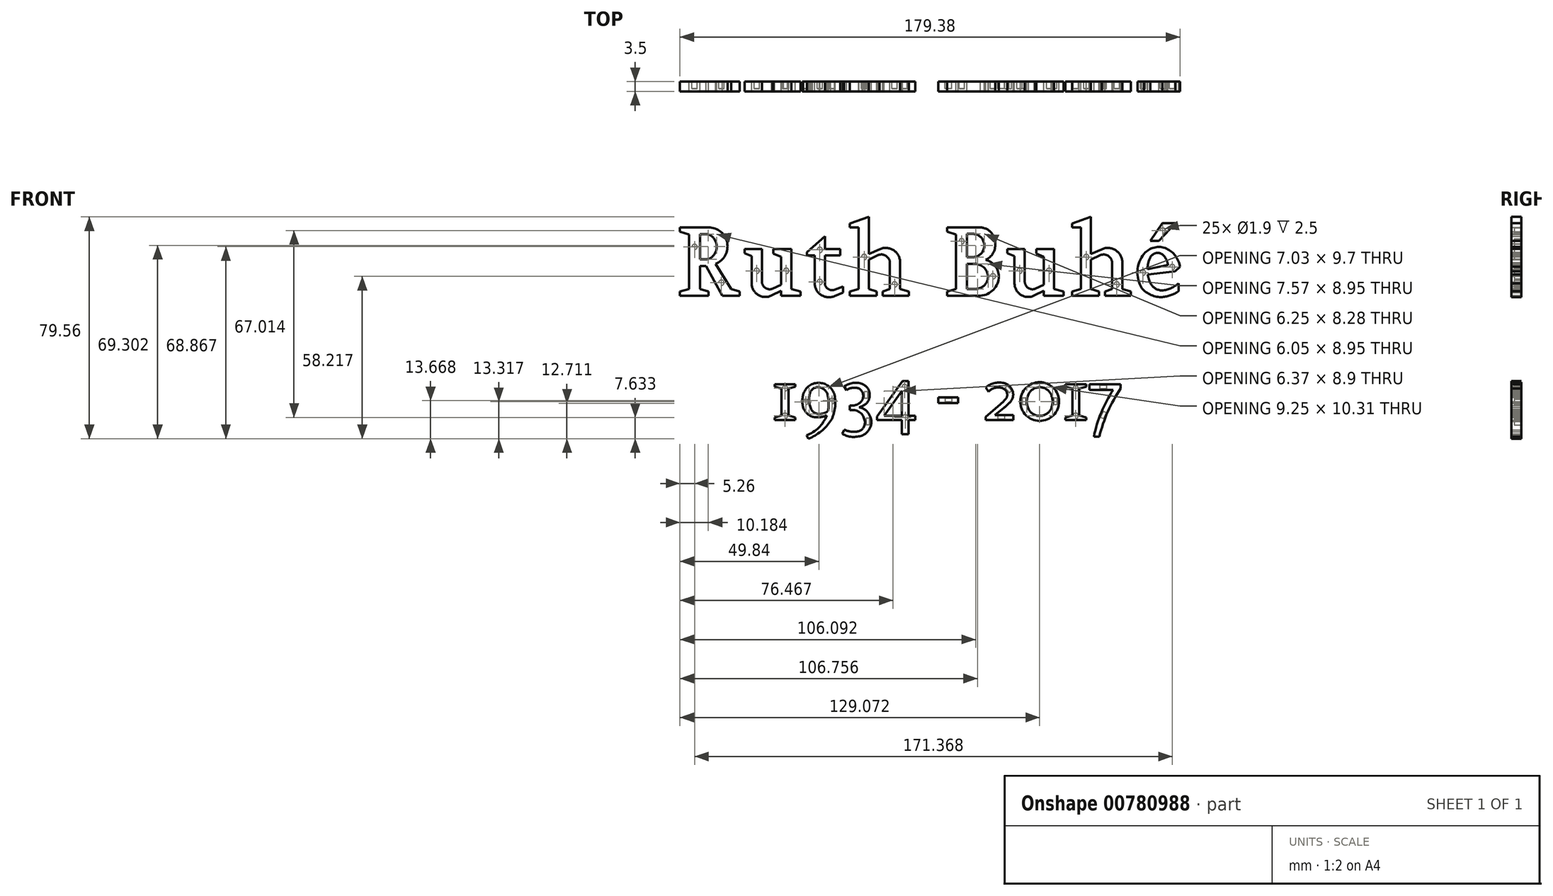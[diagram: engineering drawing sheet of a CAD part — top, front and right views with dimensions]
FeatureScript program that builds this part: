
annotation { "Feature Type Name" : "Feature", "Feature Type Description" : "" }
export const myFeature = defineFeature(function(context is Context, id is Id, definition is map)
    precondition{}
    {
        {
            var Q0;
            Q0=qCreatedBy(makeId("Front.planeOp"),FACE);
            var sketch = newSketch(context, id + "F0", { "sketchPlane" : qUnion([Q0])});
            skSolve(sketch);
        }
        {
            var Q0;
            Q0=qCreatedBy(makeId("Front.planeOp"),FACE);
            var sketch = newSketch(context, id + "F1", { "sketchPlane" : qUnion([Q0])});
            skLineSegment(sketch, "E0", {"start": v(-78.02, 15.2) * mm, "end": v(-67.8, 15.2) * mm});
            skLineSegment(sketch, "E1", {"start": v(-67.8, 15.2) * mm, "end": v(-67.8, 16.73) * mm});
            skLineSegment(sketch, "E2", {"start": v(-67.8, 16.73) * mm, "end": v(-70.86, 17.67) * mm});
            skLineSegment(sketch, "E3", {"start": v(-70.86, 17.67) * mm, "end": v(-70.86, 25.9) * mm});
            skLineSegment(sketch, "E4", {"start": v(-70.86, 25.9) * mm, "end": v(-68.64, 25.9) * mm});
            skLineSegment(sketch, "E5", {"start": v(-68.64, 25.9) * mm, "end": v(-62.81, 15.2) * mm});
            skLineSegment(sketch, "E6", {"start": v(-62.81, 15.2) * mm, "end": v(-56.63, 15.2) * mm});
            skLineSegment(sketch, "E7", {"start": v(-56.63, 15.2) * mm, "end": v(-56.63, 16.73) * mm});
            skLineSegment(sketch, "E8", {"start": v(-56.63, 16.73) * mm, "end": v(-59.61, 17.67) * mm});
            skLineSegment(sketch, "E9", {"start": v(-59.61, 17.67) * mm, "end": v(-65.23, 26.62) * mm});
            skLineSegment(sketch, "E10", {"start": v(-78.02, 15.2) * mm, "end": v(-78.02, 16.73) * mm});
            skLineSegment(sketch, "E11", {"start": v(-78.02, 16.73) * mm, "end": v(-74.74, 17.67) * mm});
            skLineSegment(sketch, "E12", {"start": v(-74.74, 17.67) * mm, "end": v(-74.74, 37.23) * mm});
            skLineSegment(sketch, "E13", {"start": v(-74.74, 37.23) * mm, "end": v(-78.02, 38.21) * mm});
            skLineSegment(sketch, "E14", {"start": v(-78.02, 38.21) * mm, "end": v(-78.02, 39.74) * mm});
            skLineSegment(sketch, "E15", {"start": v(-78.02, 39.74) * mm, "end": v(-68.86, 39.74) * mm});
            skArc(sketch, "E16", {"start": v(-65.23, 26.62) * mm, "mid": v(-61.06, 34.23) * mm, "end": v(-67.76, 39.74) * mm});
            skArc(sketch, "E17", {"start": v(-67.74, 28.32) * mm, "mid": v(-64.81, 32.8) * mm, "end": v(-67.74, 37.27) * mm});
            skLineSegment(sketch, "E18", {"start": v(-67.74, 37.27) * mm, "end": v(-70.86, 37.27) * mm});
            skLineSegment(sketch, "E19", {"start": v(-70.86, 37.27) * mm, "end": v(-70.86, 28.32) * mm});
            skLineSegment(sketch, "E20", {"start": v(-70.86, 28.32) * mm, "end": v(-67.74, 28.32) * mm});
            skLineSegment(sketch, "E21", {"start": v(-68.86, 39.74) * mm, "end": v(-67.76, 39.74) * mm});
            skSolve(sketch);
        }
        {
            var Q0;
            Q0=makeQuery(id+"F1.imprint","IMPRINT",FACE,{"disambiguationData":[TD([[makeQuery(id+"F1.imprint","IMPRINT",EDGE,{"derivedFrom":sQuery(id+"F1.wireOp",EDGE,"E0")}),1.0]])]});
            extrude(context, id + "F2", {"entities" : qUnion([Q0]), "depth" : 3.5 * mm, "offsetDistance" : 25 * mm});
        }
        {
            var Q0;
            Q0=makeQuery(id+"F2.opExtrude","SWEPT_EDGE",EDGE,{"disambiguationData":[OSD([sQuery(id+"F1.wireOp",EDGE,"E17"),sQuery(id+"F1.wireOp",EDGE,"E18")])]});
            var Q1;
            Q1=makeQuery(id+"F2.opExtrude","SWEPT_EDGE",EDGE,{"disambiguationData":[OSD([sQuery(id+"F1.wireOp",EDGE,"E17"),sQuery(id+"F1.wireOp",EDGE,"E20")])]});
            fillet(context, id + "F3", {"entities" : qUnion([Q0, Q1]), "radius" : 3 * mm, "tangentPropagation" : true, "allowEdgeOverflow" : false});
        }
        {
            var Q0;
            Q0=makeQuery(id+"F2.opExtrude","CAP_FACE",FACE,{"disambiguationData":[OSD([sQuery(id+"F1.wireOp",EDGE,"E0"),sQuery(id+"F1.wireOp",EDGE,"E1"),sQuery(id+"F1.wireOp",EDGE,"E2"),sQuery(id+"F1.wireOp",EDGE,"E3"),sQuery(id+"F1.wireOp",EDGE,"E4"),sQuery(id+"F1.wireOp",EDGE,"E5"),sQuery(id+"F1.wireOp",EDGE,"E6"),sQuery(id+"F1.wireOp",EDGE,"E7"),sQuery(id+"F1.wireOp",EDGE,"E8"),sQuery(id+"F1.wireOp",EDGE,"E9"),sQuery(id+"F1.wireOp",EDGE,"E10"),sQuery(id+"F1.wireOp",EDGE,"E11"),sQuery(id+"F1.wireOp",EDGE,"E12"),sQuery(id+"F1.wireOp",EDGE,"E13"),sQuery(id+"F1.wireOp",EDGE,"E14"),sQuery(id+"F1.wireOp",EDGE,"E15"),sQuery(id+"F1.wireOp",EDGE,"E16"),sQuery(id+"F1.wireOp",EDGE,"E17"),sQuery(id+"F1.wireOp",EDGE,"E18"),sQuery(id+"F1.wireOp",EDGE,"E19"),sQuery(id+"F1.wireOp",EDGE,"E20"),sQuery(id+"F1.wireOp",EDGE,"E21")])],"isStart":true});
            var sketch = newSketch(context, id + "F4", { "sketchPlane" : qUnion([Q0])});
            skCircle(sketch, "E22", {"center": v(72.76, 32.74) * mm, "radius": 0.95 * mm});
            skCircle(sketch, "E23", {"center": v(63.13, 19.9) * mm, "radius": 0.95 * mm});
            skSolve(sketch);
        }
        {
            var Q0;
            Q0=makeQuery(id+"F4.imprint","IMPRINT",FACE,{"disambiguationData":[TD([[makeQuery(id+"F4.imprint","IMPRINT",EDGE,{"derivedFrom":sQuery(id+"F4.wireOp",EDGE,"E22")}),1.0]])]});
            var Q1;
            Q1=makeQuery(id+"F4.imprint","IMPRINT",FACE,{"disambiguationData":[TD([[makeQuery(id+"F4.imprint","IMPRINT",EDGE,{"derivedFrom":sQuery(id+"F4.wireOp",EDGE,"E23")}),1.0]])]});
            extrude(context, id + "F5", {"entities" : qUnion([Q0, Q1]), "operationType" : NewBodyOperationType.REMOVE, "oppositeDirection" : true, "depth" : 2.5 * mm, "offsetDistance" : 25 * mm});
        }
        {
            var Q0;
            Q0=qCreatedBy(makeId("Front.planeOp"),FACE);
            var sketch = newSketch(context, id + "F6", { "sketchPlane" : qUnion([Q0])});
            skLineSegment(sketch, "E24", {"start": v(-41.77, 15.2) * mm, "end": v(-34.7, 15.2) * mm});
            skLineSegment(sketch, "E25", {"start": v(-34.7, 15.2) * mm, "end": v(-34.7, 16.73) * mm});
            skLineSegment(sketch, "E26", {"start": v(-34.7, 16.73) * mm, "end": v(-38.08, 17.67) * mm});
            skLineSegment(sketch, "E27", {"start": v(-38.08, 17.67) * mm, "end": v(-38.08, 32) * mm});
            skLineSegment(sketch, "E28", {"start": v(-38.08, 32) * mm, "end": v(-44.47, 32) * mm});
            skLineSegment(sketch, "E29", {"start": v(-44.47, 32) * mm, "end": v(-44.47, 30.27) * mm});
            skLineSegment(sketch, "E30", {"start": v(-44.47, 30.27) * mm, "end": v(-41.77, 29.18) * mm});
            skLineSegment(sketch, "E31", {"start": v(-41.77, 29.18) * mm, "end": v(-41.77, 19.11) * mm});
            skLineSegment(sketch, "E32", {"start": v(-41.77, 15.2) * mm, "end": v(-41.77, 16.98) * mm});
            skLineSegment(sketch, "E33", {"start": v(-41.77, 16.98) * mm, "end": v(-45.17, 15.3) * mm});
            skLineSegment(sketch, "E34", {"start": v(-41.77, 19.11) * mm, "end": v(-44.76, 17.72) * mm});
            skLineSegment(sketch, "E35", {"start": v(-52.26, 19.48) * mm, "end": v(-52.26, 29.48) * mm});
            skLineSegment(sketch, "E36", {"start": v(-52.26, 29.48) * mm, "end": v(-54.82, 30.46) * mm});
            skLineSegment(sketch, "E37", {"start": v(-54.82, 30.46) * mm, "end": v(-54.82, 32) * mm});
            skLineSegment(sketch, "E38", {"start": v(-54.82, 32) * mm, "end": v(-48.6, 32) * mm});
            skLineSegment(sketch, "E39", {"start": v(-48.6, 32) * mm, "end": v(-48.6, 20.2) * mm});
            skArc(sketch, "E40", {"start": v(-52.26, 19.48) * mm, "mid": v(-49.87, 15.44) * mm, "end": v(-45.17, 15.3) * mm});
            skArc(sketch, "E41", {"start": v(-48.6, 20.2) * mm, "mid": v(-47.31, 17.98) * mm, "end": v(-44.76, 17.72) * mm});
            skSolve(sketch);
        }
        {
            var Q0;
            Q0=makeQuery(id+"F6.imprint","IMPRINT",FACE,{"disambiguationData":[TD([[makeQuery(id+"F6.imprint","IMPRINT",EDGE,{"derivedFrom":sQuery(id+"F6.wireOp",EDGE,"E24")}),1.0]])]});
            extrude(context, id + "F7", {"entities" : qUnion([Q0]), "depth" : 3.5 * mm, "offsetDistance" : 25 * mm});
        }
        {
            var Q0;
            Q0=makeQuery(id+"F7.opExtrude","CAP_FACE",FACE,{"disambiguationData":[OSD([sQuery(id+"F6.wireOp",EDGE,"E24"),sQuery(id+"F6.wireOp",EDGE,"E25"),sQuery(id+"F6.wireOp",EDGE,"E26"),sQuery(id+"F6.wireOp",EDGE,"E27"),sQuery(id+"F6.wireOp",EDGE,"E28"),sQuery(id+"F6.wireOp",EDGE,"E29"),sQuery(id+"F6.wireOp",EDGE,"E30"),sQuery(id+"F6.wireOp",EDGE,"E31"),sQuery(id+"F6.wireOp",EDGE,"E32"),sQuery(id+"F6.wireOp",EDGE,"E33"),sQuery(id+"F6.wireOp",EDGE,"E34"),sQuery(id+"F6.wireOp",EDGE,"E35"),sQuery(id+"F6.wireOp",EDGE,"E36"),sQuery(id+"F6.wireOp",EDGE,"E37"),sQuery(id+"F6.wireOp",EDGE,"E38"),sQuery(id+"F6.wireOp",EDGE,"E39"),sQuery(id+"F6.wireOp",EDGE,"E40"),sQuery(id+"F6.wireOp",EDGE,"E41")])],"isStart":true});
            var sketch = newSketch(context, id + "F8", { "sketchPlane" : qUnion([Q0])});
            skCircle(sketch, "E42", {"center": v(50.45, 24.15) * mm, "radius": 0.95 * mm});
            skCircle(sketch, "E43", {"center": v(39.88, 24.15) * mm, "radius": 0.95 * mm});
            skPoint(sketch, "E43.centerSnap0", {"position": v(41.77, 24.15) * mm});
            skSolve(sketch);
        }
        {
            var Q0;
            Q0=makeQuery(id+"F8.imprint","IMPRINT",FACE,{"disambiguationData":[TD([[makeQuery(id+"F8.imprint","IMPRINT",EDGE,{"derivedFrom":sQuery(id+"F8.wireOp",EDGE,"E43")}),1.0]])]});
            var Q1;
            Q1=makeQuery(id+"F8.imprint","IMPRINT",FACE,{"disambiguationData":[TD([[makeQuery(id+"F8.imprint","IMPRINT",EDGE,{"derivedFrom":sQuery(id+"F8.wireOp",EDGE,"E42")}),1.0]])]});
            extrude(context, id + "F9", {"entities" : qUnion([Q0, Q1]), "operationType" : NewBodyOperationType.REMOVE, "oppositeDirection" : true, "depth" : 2.5 * mm, "offsetDistance" : 25 * mm});
        }
        {
            var Q0;
            Q0=qCreatedBy(makeId("Front.planeOp"),FACE);
            var sketch = newSketch(context, id + "F10", { "sketchPlane" : qUnion([Q0])});
            skLineSegment(sketch, "E44", {"start": v(-20.57, 32) * mm, "end": v(-26.02, 32) * mm});
            skLineSegment(sketch, "E45", {"start": v(-26.02, 32) * mm, "end": v(-26.02, 36.51) * mm});
            skLineSegment(sketch, "E46", {"start": v(-26.02, 36.51) * mm, "end": v(-32.46, 30.8) * mm});
            skLineSegment(sketch, "E47", {"start": v(-32.46, 30.8) * mm, "end": v(-32.46, 29.66) * mm});
            skLineSegment(sketch, "E48", {"start": v(-32.46, 29.66) * mm, "end": v(-29.69, 29.66) * mm});
            skLineSegment(sketch, "E49", {"start": v(-29.69, 29.66) * mm, "end": v(-29.69, 19.66) * mm});
            skLineSegment(sketch, "E50", {"start": v(-20.57, 32) * mm, "end": v(-20.57, 29.66) * mm});
            skLineSegment(sketch, "E51", {"start": v(-20.57, 29.66) * mm, "end": v(-26.02, 29.66) * mm});
            skLineSegment(sketch, "E52", {"start": v(-26.02, 29.66) * mm, "end": v(-26.02, 19.66) * mm});
            skLineSegment(sketch, "E53", {"start": v(-22.55, 17.37) * mm, "end": v(-19.53, 18.45) * mm});
            skLineSegment(sketch, "E54", {"start": v(-19.53, 18.45) * mm, "end": v(-19.53, 16.4) * mm});
            skLineSegment(sketch, "E55", {"start": v(-19.53, 16.4) * mm, "end": v(-22.56, 15.09) * mm});
            skArc(sketch, "E56", {"start": v(-29.69, 19.66) * mm, "mid": v(-27.34, 15.48) * mm, "end": v(-22.56, 15.09) * mm});
            skArc(sketch, "E57", {"start": v(-26.02, 19.66) * mm, "mid": v(-24.85, 17.65) * mm, "end": v(-22.55, 17.37) * mm});
            skSolve(sketch);
        }
        {
            var Q0;
            Q0=makeQuery(id+"F10.imprint","IMPRINT",FACE,{"disambiguationData":[TD([[makeQuery(id+"F10.imprint","IMPRINT",EDGE,{"derivedFrom":sQuery(id+"F10.wireOp",EDGE,"E44")}),1.0]])]});
            extrude(context, id + "F11", {"entities" : qUnion([Q0]), "depth" : 3.5 * mm, "offsetDistance" : 25 * mm});
        }
        {
            var Q0;
            Q0=makeQuery(id+"F11.opExtrude","CAP_FACE",FACE,{"disambiguationData":[OSD([sQuery(id+"F10.wireOp",EDGE,"E44"),sQuery(id+"F10.wireOp",EDGE,"E45"),sQuery(id+"F10.wireOp",EDGE,"E46"),sQuery(id+"F10.wireOp",EDGE,"E47"),sQuery(id+"F10.wireOp",EDGE,"E48"),sQuery(id+"F10.wireOp",EDGE,"E49"),sQuery(id+"F10.wireOp",EDGE,"E50"),sQuery(id+"F10.wireOp",EDGE,"E51"),sQuery(id+"F10.wireOp",EDGE,"E52"),sQuery(id+"F10.wireOp",EDGE,"E53"),sQuery(id+"F10.wireOp",EDGE,"E54"),sQuery(id+"F10.wireOp",EDGE,"E55"),sQuery(id+"F10.wireOp",EDGE,"E56"),sQuery(id+"F10.wireOp",EDGE,"E57")])],"isStart":true});
            var sketch = newSketch(context, id + "F12", { "sketchPlane" : qUnion([Q0])});
            skCircle(sketch, "E58", {"center": v(27.83, 31.66) * mm, "radius": 0.95 * mm});
            skCircle(sketch, "E59", {"center": v(27.83, 20.16) * mm, "radius": 0.95 * mm});
            skSolve(sketch);
        }
        {
            var Q0;
            Q0=makeQuery(id+"F12.imprint","IMPRINT",FACE,{"disambiguationData":[TD([[makeQuery(id+"F12.imprint","IMPRINT",EDGE,{"derivedFrom":sQuery(id+"F12.wireOp",EDGE,"E58")}),1.0]])]});
            var Q1;
            Q1=makeQuery(id+"F12.imprint","IMPRINT",FACE,{"disambiguationData":[TD([[makeQuery(id+"F12.imprint","IMPRINT",EDGE,{"derivedFrom":sQuery(id+"F12.wireOp",EDGE,"E59")}),1.0]])]});
            extrude(context, id + "F13", {"entities" : qUnion([Q0, Q1]), "operationType" : NewBodyOperationType.REMOVE, "oppositeDirection" : true, "depth" : 2.5 * mm, "offsetDistance" : 25 * mm});
        }
        {
            var Q0;
            Q0=qCreatedBy(makeId("Front.planeOp"),FACE);
            var sketch = newSketch(context, id + "F14", { "sketchPlane" : qUnion([Q0])});
            skLineSegment(sketch, "E60", {"start": v(-17.06, 15.2) * mm, "end": v(-7.42, 15.2) * mm});
            skLineSegment(sketch, "E61", {"start": v(-7.42, 15.2) * mm, "end": v(-7.42, 16.73) * mm});
            skLineSegment(sketch, "E62", {"start": v(-7.42, 16.73) * mm, "end": v(-10.26, 17.67) * mm});
            skLineSegment(sketch, "E63", {"start": v(-10.26, 17.67) * mm, "end": v(-10.26, 28.2) * mm});
            skLineSegment(sketch, "E64", {"start": v(-10.26, 28.2) * mm, "end": v(-6.9, 29.76) * mm});
            skLineSegment(sketch, "E65", {"start": v(-17.06, 15.2) * mm, "end": v(-17.06, 16.73) * mm});
            skLineSegment(sketch, "E66", {"start": v(-17.06, 16.73) * mm, "end": v(-13.88, 17.67) * mm});
            skLineSegment(sketch, "E67", {"start": v(-13.88, 17.67) * mm, "end": v(-13.88, 39.74) * mm});
            skLineSegment(sketch, "E68", {"start": v(-13.88, 39.74) * mm, "end": v(-17.06, 39.74) * mm});
            skLineSegment(sketch, "E69", {"start": v(-17.06, 39.74) * mm, "end": v(-17.06, 41.1) * mm});
            skLineSegment(sketch, "E70", {"start": v(-17.06, 41.1) * mm, "end": v(-10.26, 43.5) * mm});
            skLineSegment(sketch, "E71", {"start": v(-10.26, 43.5) * mm, "end": v(-10.26, 30.24) * mm});
            skLineSegment(sketch, "E72", {"start": v(-10.26, 30.24) * mm, "end": v(-6.4, 31.9) * mm});
            skLineSegment(sketch, "E73", {"start": v(-2.67, 27.17) * mm, "end": v(-2.67, 17.67) * mm});
            skLineSegment(sketch, "E74", {"start": v(-2.67, 17.67) * mm, "end": v(-5.22, 16.73) * mm});
            skLineSegment(sketch, "E75", {"start": v(-5.22, 16.73) * mm, "end": v(-5.22, 15.2) * mm});
            skLineSegment(sketch, "E76", {"start": v(-5.22, 15.2) * mm, "end": v(4.1, 15.2) * mm});
            skLineSegment(sketch, "E77", {"start": v(4.1, 15.2) * mm, "end": v(4.1, 16.73) * mm});
            skLineSegment(sketch, "E78", {"start": v(4.1, 16.73) * mm, "end": v(0.99, 17.67) * mm});
            skLineSegment(sketch, "E79", {"start": v(0.99, 17.67) * mm, "end": v(0.99, 27.07) * mm});
            skArc(sketch, "E80", {"start": v(0.99, 27.07) * mm, "mid": v(-1.37, 31.53) * mm, "end": v(-6.4, 31.9) * mm});
            skArc(sketch, "E81", {"start": v(-2.67, 27.17) * mm, "mid": v(-4.12, 29.56) * mm, "end": v(-6.9, 29.76) * mm});
            skSolve(sketch);
        }
        {
            var Q0;
            Q0=makeQuery(id+"F14.imprint","IMPRINT",FACE,{"disambiguationData":[TD([[makeQuery(id+"F14.imprint","IMPRINT",EDGE,{"derivedFrom":sQuery(id+"F14.wireOp",EDGE,"E60")}),1.0]])]});
            extrude(context, id + "F15", {"entities" : qUnion([Q0]), "depth" : 3.5 * mm, "offsetDistance" : 25 * mm});
        }
        {
            var Q0;
            Q0=makeQuery(id+"F15.opExtrude","CAP_FACE",FACE,{"disambiguationData":[OSD([sQuery(id+"F14.wireOp",EDGE,"E60"),sQuery(id+"F14.wireOp",EDGE,"E61"),sQuery(id+"F14.wireOp",EDGE,"E62"),sQuery(id+"F14.wireOp",EDGE,"E63"),sQuery(id+"F14.wireOp",EDGE,"E64"),sQuery(id+"F14.wireOp",EDGE,"E65"),sQuery(id+"F14.wireOp",EDGE,"E66"),sQuery(id+"F14.wireOp",EDGE,"E67"),sQuery(id+"F14.wireOp",EDGE,"E68"),sQuery(id+"F14.wireOp",EDGE,"E69"),sQuery(id+"F14.wireOp",EDGE,"E70"),sQuery(id+"F14.wireOp",EDGE,"E71"),sQuery(id+"F14.wireOp",EDGE,"E72"),sQuery(id+"F14.wireOp",EDGE,"E73"),sQuery(id+"F14.wireOp",EDGE,"E74"),sQuery(id+"F14.wireOp",EDGE,"E75"),sQuery(id+"F14.wireOp",EDGE,"E76"),sQuery(id+"F14.wireOp",EDGE,"E77"),sQuery(id+"F14.wireOp",EDGE,"E78"),sQuery(id+"F14.wireOp",EDGE,"E79"),sQuery(id+"F14.wireOp",EDGE,"E80"),sQuery(id+"F14.wireOp",EDGE,"E81")])],"isStart":true});
            var sketch = newSketch(context, id + "F16", { "sketchPlane" : qUnion([Q0])});
            skCircle(sketch, "E82", {"center": v(11.93, 29.1) * mm, "radius": 0.95 * mm});
            skCircle(sketch, "E83", {"center": v(0.99, 19.26) * mm, "radius": 0.95 * mm});
            skSolve(sketch);
        }
        {
            var Q0;
            Q0=makeQuery(id+"F16.imprint","IMPRINT",FACE,{"disambiguationData":[TD([[makeQuery(id+"F16.imprint","IMPRINT",EDGE,{"derivedFrom":sQuery(id+"F16.wireOp",EDGE,"E83")}),1.0]])]});
            var Q1;
            Q1=makeQuery(id+"F16.imprint","IMPRINT",FACE,{"disambiguationData":[TD([[makeQuery(id+"F16.imprint","IMPRINT",EDGE,{"derivedFrom":sQuery(id+"F16.wireOp",EDGE,"E82")}),1.0]])]});
            extrude(context, id + "F17", {"entities" : qUnion([Q0, Q1]), "operationType" : NewBodyOperationType.REMOVE, "oppositeDirection" : true, "depth" : 2.5 * mm, "offsetDistance" : 25 * mm});
        }
        {
            var Q0;
            Q0=qCreatedBy(makeId("Front.planeOp"),FACE);
            var sketch = newSketch(context, id + "F18", { "sketchPlane" : qUnion([Q0])});
            skLineSegment(sketch, "E84", {"start": v(29.79, 15.2) * mm, "end": v(17.79, 15.2) * mm});
            skLineSegment(sketch, "E85", {"start": v(17.79, 15.2) * mm, "end": v(17.79, 16.73) * mm});
            skLineSegment(sketch, "E86", {"start": v(17.79, 16.73) * mm, "end": v(21.07, 17.67) * mm});
            skLineSegment(sketch, "E87", {"start": v(21.07, 17.67) * mm, "end": v(21.07, 37.23) * mm});
            skLineSegment(sketch, "E88", {"start": v(21.07, 37.23) * mm, "end": v(17.79, 38.21) * mm});
            skLineSegment(sketch, "E89", {"start": v(17.79, 38.21) * mm, "end": v(17.79, 39.74) * mm});
            skLineSegment(sketch, "E90", {"start": v(17.79, 39.74) * mm, "end": v(29.42, 39.74) * mm});
            skLineSegment(sketch, "E91", {"start": v(27.65, 37.37) * mm, "end": v(24.95, 37.37) * mm});
            skLineSegment(sketch, "E92", {"start": v(24.95, 37.37) * mm, "end": v(24.95, 29.1) * mm});
            skLineSegment(sketch, "E93", {"start": v(24.95, 29.1) * mm, "end": v(27.65, 29.1) * mm});
            skLineSegment(sketch, "E94", {"start": v(27.84, 26.62) * mm, "end": v(24.95, 26.62) * mm});
            skLineSegment(sketch, "E95", {"start": v(24.95, 26.62) * mm, "end": v(24.95, 17.67) * mm});
            skLineSegment(sketch, "E96", {"start": v(24.95, 17.67) * mm, "end": v(28.14, 17.67) * mm});
            skArc(sketch, "E97", {"start": v(35.13, 33.82) * mm, "mid": v(33.53, 38) * mm, "end": v(29.42, 39.74) * mm});
            skArc(sketch, "E98", {"start": v(31.72, 28.11) * mm, "mid": v(34.29, 30.45) * mm, "end": v(35.13, 33.82) * mm});
            skArc(sketch, "E99", {"start": v(36.45, 22.2) * mm, "mid": v(35.03, 25.92) * mm, "end": v(31.72, 28.11) * mm});
            skArc(sketch, "E100", {"start": v(29.79, 15.2) * mm, "mid": v(34.49, 17.4) * mm, "end": v(36.45, 22.2) * mm});
            skArc(sketch, "E101", {"start": v(32.52, 22.31) * mm, "mid": v(31.02, 25.38) * mm, "end": v(27.84, 26.62) * mm});
            skArc(sketch, "E102", {"start": v(28.14, 17.67) * mm, "mid": v(31.33, 19.05) * mm, "end": v(32.52, 22.31) * mm});
            skArc(sketch, "E103", {"start": v(27.65, 29.1) * mm, "mid": v(31.2, 33.23) * mm, "end": v(27.65, 37.37) * mm});
            skSolve(sketch);
        }
        {
            var Q0;
            Q0=makeQuery(id+"F18.imprint","IMPRINT",FACE,{"disambiguationData":[TD([[makeQuery(id+"F18.imprint","IMPRINT",EDGE,{"derivedFrom":sQuery(id+"F18.wireOp",EDGE,"E84")}),-1.0]])]});
            extrude(context, id + "F19", {"entities" : qUnion([Q0]), "depth" : 3.5 * mm, "offsetDistance" : 25 * mm});
        }
        {
            var Q0;
            Q0=makeQuery(id+"F19.opExtrude","SWEPT_EDGE",EDGE,{"disambiguationData":[OSD([sQuery(id+"F18.wireOp",EDGE,"E91"),sQuery(id+"F18.wireOp",EDGE,"E103")])]});
            var Q1;
            Q1=makeQuery(id+"F19.opExtrude","SWEPT_EDGE",EDGE,{"disambiguationData":[OSD([sQuery(id+"F18.wireOp",EDGE,"E93"),sQuery(id+"F18.wireOp",EDGE,"E103")])]});
            fillet(context, id + "F20", {"entities" : qUnion([Q0, Q1]), "radius" : 3 * mm, "tangentPropagation" : true, "allowEdgeOverflow" : false});
        }
        {
            var Q0;
            Q0=makeQuery(id+"F19.opExtrude","CAP_FACE",FACE,{"disambiguationData":[OSD([sQuery(id+"F18.wireOp",EDGE,"E84"),sQuery(id+"F18.wireOp",EDGE,"E85"),sQuery(id+"F18.wireOp",EDGE,"E86"),sQuery(id+"F18.wireOp",EDGE,"E87"),sQuery(id+"F18.wireOp",EDGE,"E88"),sQuery(id+"F18.wireOp",EDGE,"E89"),sQuery(id+"F18.wireOp",EDGE,"E90"),sQuery(id+"F18.wireOp",EDGE,"E91"),sQuery(id+"F18.wireOp",EDGE,"E92"),sQuery(id+"F18.wireOp",EDGE,"E93"),sQuery(id+"F18.wireOp",EDGE,"E94"),sQuery(id+"F18.wireOp",EDGE,"E95"),sQuery(id+"F18.wireOp",EDGE,"E96"),sQuery(id+"F18.wireOp",EDGE,"E97"),sQuery(id+"F18.wireOp",EDGE,"E98"),sQuery(id+"F18.wireOp",EDGE,"E99"),sQuery(id+"F18.wireOp",EDGE,"E100"),sQuery(id+"F18.wireOp",EDGE,"E101"),sQuery(id+"F18.wireOp",EDGE,"E102"),sQuery(id+"F18.wireOp",EDGE,"E103")])],"isStart":true});
            var sketch = newSketch(context, id + "F21", { "sketchPlane" : qUnion([Q0])});
            skCircle(sketch, "E104", {"center": v(-23.07, 34.74) * mm, "radius": 0.95 * mm});
            skCircle(sketch, "E105", {"center": v(-34.29, 22.2) * mm, "radius": 0.95 * mm});
            skSolve(sketch);
        }
        {
            var Q0;
            Q0=makeQuery(id+"F21.imprint","IMPRINT",FACE,{"disambiguationData":[TD([[makeQuery(id+"F21.imprint","IMPRINT",EDGE,{"derivedFrom":sQuery(id+"F21.wireOp",EDGE,"E105")}),1.0]])]});
            var Q1;
            Q1=makeQuery(id+"F21.imprint","IMPRINT",FACE,{"disambiguationData":[TD([[makeQuery(id+"F21.imprint","IMPRINT",EDGE,{"derivedFrom":sQuery(id+"F21.wireOp",EDGE,"E104")}),1.0]])]});
            extrude(context, id + "F22", {"entities" : qUnion([Q0, Q1]), "operationType" : NewBodyOperationType.REMOVE, "oppositeDirection" : true, "depth" : 2.5 * mm, "offsetDistance" : 25 * mm});
        }
        {
            var Q0;
            Q0=qCreatedBy(makeId("Front.planeOp"),FACE);
            var sketch = newSketch(context, id + "F23", { "sketchPlane" : qUnion([Q0])});
            skLineSegment(sketch, "E106", {"start": v(90.8, 34.88) * mm, "end": v(93.74, 34.88) * mm});
            skLineSegment(sketch, "E107", {"start": v(93.74, 34.88) * mm, "end": v(99.81, 41.18) * mm});
            skLineSegment(sketch, "E108", {"start": v(99.81, 41.18) * mm, "end": v(95.06, 41.18) * mm});
            skLineSegment(sketch, "E109", {"start": v(95.06, 41.18) * mm, "end": v(90.8, 34.88) * mm});
            skLineSegment(sketch, "E110", {"start": v(99.7, 23.95) * mm, "end": v(101.36, 25.66) * mm});
            skArc(sketch, "E111", {"start": v(101.36, 25.66) * mm, "mid": v(99.76, 29.5) * mm, "end": v(96.55, 32.12) * mm});
            skArc(sketch, "E112", {"start": v(96.55, 32.12) * mm, "mid": v(92.2, 32.52) * mm, "end": v(88.49, 30.24) * mm});
            skArc(sketch, "E113", {"start": v(88.49, 30.24) * mm, "mid": v(86.13, 24.18) * mm, "end": v(87.72, 17.87) * mm});
            skArc(sketch, "E114", {"start": v(87.72, 17.87) * mm, "mid": v(91.03, 15.46) * mm, "end": v(95.06, 14.72) * mm});
            skArc(sketch, "E115", {"start": v(95.06, 14.72) * mm, "mid": v(98.1, 15.4) * mm, "end": v(100.86, 16.82) * mm});
            skLineSegment(sketch, "E116", {"start": v(100.86, 16.82) * mm, "end": v(100.86, 19.7) * mm});
            skArc(sketch, "E117", {"start": v(94.95, 17.1) * mm, "mid": v(98.11, 17.92) * mm, "end": v(100.86, 19.7) * mm});
            skArc(sketch, "E118", {"start": v(90.8, 19.7) * mm, "mid": v(92.53, 17.83) * mm, "end": v(94.95, 17.1) * mm});
            skArc(sketch, "E119", {"start": v(90.8, 29.14) * mm, "mid": v(89.98, 26.84) * mm, "end": v(89.7, 24.42) * mm});
            skArc(sketch, "E120", {"start": v(95.94, 29.14) * mm, "mid": v(93.38, 30.56) * mm, "end": v(90.8, 29.14) * mm});
            skArc(sketch, "E121", {"start": v(97.1, 26.21) * mm, "mid": v(96.68, 27.74) * mm, "end": v(95.94, 29.14) * mm});
            skLineSegment(sketch, "E122", {"start": v(99.7, 23.95) * mm, "end": v(89.81, 22.85) * mm});
            skLineSegment(sketch, "E123", {"start": v(97.1, 26.21) * mm, "end": v(89.7, 24.76) * mm});
            skPoint(sketch, "E123.endSnap0", {"position": v(89.7, 24.42) * mm});
            skArc(sketch, "E124.trimOffspring", {"start": v(89.81, 22.85) * mm, "mid": v(90.19, 21.23) * mm, "end": v(90.8, 19.7) * mm});
            skPoint(sketch, "E125.orphan", {"position": v(87.94, 24.42) * mm});
            skSolve(sketch);
        }
        {
            var Q0;
            Q0=makeQuery(id+"F23.imprint","IMPRINT",FACE,{"disambiguationData":[TD([[makeQuery(id+"F23.imprint","IMPRINT",EDGE,{"derivedFrom":sQuery(id+"F23.wireOp",EDGE,"E110")}),1.0]])]});
            var Q1;
            Q1=makeQuery(id+"F23.imprint","IMPRINT",FACE,{"disambiguationData":[TD([[makeQuery(id+"F23.imprint","IMPRINT",EDGE,{"derivedFrom":sQuery(id+"F23.wireOp",EDGE,"E106")}),1.0]])]});
            extrude(context, id + "F24", {"entities" : qUnion([Q0, Q1]), "depth" : 3.5 * mm, "offsetDistance" : 25 * mm});
        }
        {
            var Q0;
            Q0=makeQuery(id+"F24.opExtrude","CAP_FACE",FACE,{"disambiguationData":[OSD([sQuery(id+"F23.wireOp",EDGE,"E106"),sQuery(id+"F23.wireOp",EDGE,"E107"),sQuery(id+"F23.wireOp",EDGE,"E108"),sQuery(id+"F23.wireOp",EDGE,"E109")])],"isStart":true});
            var sketch = newSketch(context, id + "F25", { "sketchPlane" : qUnion([Q0])});
            skCircle(sketch, "E126", {"center": v(-98.6, 25.5) * mm, "radius": 0.95 * mm});
            skCircle(sketch, "E127", {"center": v(-88.1, 23.5) * mm, "radius": 0.95 * mm});
            skCircle(sketch, "E128", {"center": v(-95.2, 38.58) * mm, "radius": 0.95 * mm});
            skSolve(sketch);
        }
        {
            var Q0;
            Q0=makeQuery(id+"F25.imprint","IMPRINT",FACE,{"disambiguationData":[TD([[makeQuery(id+"F25.imprint","IMPRINT",EDGE,{"derivedFrom":sQuery(id+"F25.wireOp",EDGE,"E126")}),1.0]])]});
            var Q1;
            Q1=makeQuery(id+"F25.imprint","IMPRINT",FACE,{"disambiguationData":[TD([[makeQuery(id+"F25.imprint","IMPRINT",EDGE,{"derivedFrom":sQuery(id+"F25.wireOp",EDGE,"E127")}),1.0]])]});
            extrude(context, id + "F26", {"entities" : qUnion([Q0, Q1]), "operationType" : NewBodyOperationType.REMOVE, "oppositeDirection" : true, "depth" : 2.5 * mm, "offsetDistance" : 25 * mm});
        }
        {
            var Q0;
            Q0=makeQuery(id+"F25.imprint","IMPRINT",FACE,{"disambiguationData":[TD([[makeQuery(id+"F25.imprint","IMPRINT",EDGE,{"derivedFrom":sQuery(id+"F25.wireOp",EDGE,"E128")}),1.0]])]});
            extrude(context, id + "F27", {"entities" : qUnion([Q0]), "operationType" : NewBodyOperationType.REMOVE, "oppositeDirection" : true, "depth" : 2.5 * mm, "offsetDistance" : 25 * mm});
        }
        {
            var Q0;
            Q0=makeQuery(id+"F7.opExtrude","SWEPT_BODY",BODY,{"disambiguationData":[OSD([sQuery(id+"F6.wireOp",EDGE,"E24"),sQuery(id+"F6.wireOp",EDGE,"E25"),sQuery(id+"F6.wireOp",EDGE,"E26"),sQuery(id+"F6.wireOp",EDGE,"E27"),sQuery(id+"F6.wireOp",EDGE,"E28"),sQuery(id+"F6.wireOp",EDGE,"E29"),sQuery(id+"F6.wireOp",EDGE,"E30"),sQuery(id+"F6.wireOp",EDGE,"E31"),sQuery(id+"F6.wireOp",EDGE,"E32"),sQuery(id+"F6.wireOp",EDGE,"E33"),sQuery(id+"F6.wireOp",EDGE,"E34"),sQuery(id+"F6.wireOp",EDGE,"E35"),sQuery(id+"F6.wireOp",EDGE,"E36"),sQuery(id+"F6.wireOp",EDGE,"E37"),sQuery(id+"F6.wireOp",EDGE,"E38"),sQuery(id+"F6.wireOp",EDGE,"E39"),sQuery(id+"F6.wireOp",EDGE,"E40"),sQuery(id+"F6.wireOp",EDGE,"E41")])]});
            transform(context, id + "F28", {"entities" : qUnion([Q0]), "transformType" : TransformType.TRANSLATION_3D, "dx" : 94.3 * mm, "dy" : 0 * mm, "dz" : 0 * mm, "makeCopy" : true});
        }
        {
            var Q0;
            Q0=makeQuery(id+"F15.opExtrude","SWEPT_BODY",BODY,{"disambiguationData":[OSD([sQuery(id+"F14.wireOp",EDGE,"E60"),sQuery(id+"F14.wireOp",EDGE,"E61"),sQuery(id+"F14.wireOp",EDGE,"E62"),sQuery(id+"F14.wireOp",EDGE,"E63"),sQuery(id+"F14.wireOp",EDGE,"E64"),sQuery(id+"F14.wireOp",EDGE,"E65"),sQuery(id+"F14.wireOp",EDGE,"E66"),sQuery(id+"F14.wireOp",EDGE,"E67"),sQuery(id+"F14.wireOp",EDGE,"E68"),sQuery(id+"F14.wireOp",EDGE,"E69"),sQuery(id+"F14.wireOp",EDGE,"E70"),sQuery(id+"F14.wireOp",EDGE,"E71"),sQuery(id+"F14.wireOp",EDGE,"E72"),sQuery(id+"F14.wireOp",EDGE,"E73"),sQuery(id+"F14.wireOp",EDGE,"E74"),sQuery(id+"F14.wireOp",EDGE,"E75"),sQuery(id+"F14.wireOp",EDGE,"E76"),sQuery(id+"F14.wireOp",EDGE,"E77"),sQuery(id+"F14.wireOp",EDGE,"E78"),sQuery(id+"F14.wireOp",EDGE,"E79"),sQuery(id+"F14.wireOp",EDGE,"E80"),sQuery(id+"F14.wireOp",EDGE,"E81")])]});
            transform(context, id + "F29", {"entities" : qUnion([Q0]), "transformType" : TransformType.TRANSLATION_3D, "dx" : 79.7 * mm, "dy" : 0 * mm, "dz" : 0 * mm, "makeCopy" : true});
        }
        {
            var Q0;
            Q0=qCreatedBy(makeId("Front.planeOp"),FACE);
            var sketch = newSketch(context, id + "F30", { "sketchPlane" : qUnion([Q0])});
            skLineSegment(sketch, "E129", {"start": v(-44.04, -29.35) * mm, "end": v(-36.6, -29.35) * mm});
            skLineSegment(sketch, "E130", {"start": v(-36.6, -29.35) * mm, "end": v(-36.6, -28.47) * mm});
            skLineSegment(sketch, "E131", {"start": v(-36.6, -28.47) * mm, "end": v(-39.1, -27.72) * mm});
            skLineSegment(sketch, "E132", {"start": v(-39.1, -27.72) * mm, "end": v(-39.1, -18.13) * mm});
            skLineSegment(sketch, "E133", {"start": v(-39.1, -18.13) * mm, "end": v(-36.6, -17.38) * mm});
            skLineSegment(sketch, "E134", {"start": v(-36.6, -17.38) * mm, "end": v(-36.6, -16.5) * mm});
            skLineSegment(sketch, "E135", {"start": v(-36.6, -16.5) * mm, "end": v(-44.04, -16.5) * mm});
            skLineSegment(sketch, "E136", {"start": v(-44.04, -16.5) * mm, "end": v(-44.04, -17.38) * mm});
            skLineSegment(sketch, "E137", {"start": v(-44.04, -17.38) * mm, "end": v(-41.53, -18.13) * mm});
            skLineSegment(sketch, "E138", {"start": v(-41.53, -18.13) * mm, "end": v(-41.53, -27.72) * mm});
            skLineSegment(sketch, "E139", {"start": v(-41.53, -27.72) * mm, "end": v(-44.04, -28.47) * mm});
            skLineSegment(sketch, "E140", {"start": v(-44.04, -28.47) * mm, "end": v(-44.04, -29.35) * mm});
            skSolve(sketch);
        }
        {
            var Q0;
            Q0=makeQuery(id+"F30.imprint","IMPRINT",FACE,{"disambiguationData":[TD([[makeQuery(id+"F30.imprint","IMPRINT",EDGE,{"derivedFrom":sQuery(id+"F30.wireOp",EDGE,"E129")}),1.0]])]});
            extrude(context, id + "F31", {"entities" : qUnion([Q0]), "depth" : 3.5 * mm, "offsetDistance" : 25 * mm});
        }
        {
            var Q0;
            Q0=makeQuery(id+"F31.opExtrude","CAP_FACE",FACE,{"disambiguationData":[OSD([sQuery(id+"F30.wireOp",EDGE,"E129"),sQuery(id+"F30.wireOp",EDGE,"E130"),sQuery(id+"F30.wireOp",EDGE,"E131"),sQuery(id+"F30.wireOp",EDGE,"E132"),sQuery(id+"F30.wireOp",EDGE,"E133"),sQuery(id+"F30.wireOp",EDGE,"E134"),sQuery(id+"F30.wireOp",EDGE,"E135"),sQuery(id+"F30.wireOp",EDGE,"E136"),sQuery(id+"F30.wireOp",EDGE,"E137"),sQuery(id+"F30.wireOp",EDGE,"E138"),sQuery(id+"F30.wireOp",EDGE,"E139"),sQuery(id+"F30.wireOp",EDGE,"E140")])],"isStart":true});
            var sketch = newSketch(context, id + "F32", { "sketchPlane" : qUnion([Q0])});
            skCircle(sketch, "E141", {"center": v(40.32, -18) * mm, "radius": 0.95 * mm});
            skCircle(sketch, "E142", {"center": v(40.32, -27.85) * mm, "radius": 0.95 * mm});
            skSolve(sketch);
        }
        {
            var Q0;
            Q0=makeQuery(id+"F32.imprint","IMPRINT",FACE,{"disambiguationData":[TD([[makeQuery(id+"F32.imprint","IMPRINT",EDGE,{"derivedFrom":sQuery(id+"F32.wireOp",EDGE,"E141")}),1.0]])]});
            var Q1;
            Q1=makeQuery(id+"F32.imprint","IMPRINT",FACE,{"disambiguationData":[TD([[makeQuery(id+"F32.imprint","IMPRINT",EDGE,{"derivedFrom":sQuery(id+"F32.wireOp",EDGE,"E142")}),1.0]])]});
            extrude(context, id + "F33", {"entities" : qUnion([Q0, Q1]), "operationType" : NewBodyOperationType.REMOVE, "oppositeDirection" : true, "depth" : 2.5 * mm, "offsetDistance" : 25 * mm});
        }
        {
            var Q0;
            Q0=makeQuery(id+"F31.opExtrude","SWEPT_BODY",BODY,{"disambiguationData":[OSD([sQuery(id+"F30.wireOp",EDGE,"E129"),sQuery(id+"F30.wireOp",EDGE,"E130"),sQuery(id+"F30.wireOp",EDGE,"E131"),sQuery(id+"F30.wireOp",EDGE,"E132"),sQuery(id+"F30.wireOp",EDGE,"E133"),sQuery(id+"F30.wireOp",EDGE,"E134"),sQuery(id+"F30.wireOp",EDGE,"E135"),sQuery(id+"F30.wireOp",EDGE,"E136"),sQuery(id+"F30.wireOp",EDGE,"E137"),sQuery(id+"F30.wireOp",EDGE,"E138"),sQuery(id+"F30.wireOp",EDGE,"E139"),sQuery(id+"F30.wireOp",EDGE,"E140")])]});
            transform(context, id + "F34", {"entities" : qUnion([Q0]), "transformType" : TransformType.TRANSLATION_3D, "dx" : 104.3 * mm, "dy" : 0 * mm, "dz" : 0 * mm, "makeCopy" : true});
        }
        {
            var Q0;
            Q0=qCreatedBy(makeId("Front.planeOp"),FACE);
            var sketch = newSketch(context, id + "F35", { "sketchPlane" : qUnion([Q0])});
            skLineSegment(sketch, "E143", {"start": v(3.98, -15.35) * mm, "end": v(3.98, -27.8) * mm});
            skLineSegment(sketch, "E144", {"start": v(3.98, -34.4) * mm, "end": v(1.63, -34.4) * mm});
            skLineSegment(sketch, "E145", {"start": v(1.63, -34.4) * mm, "end": v(1.63, -29.38) * mm});
            skLineSegment(sketch, "E146", {"start": v(1.63, -18.9) * mm, "end": v(-4.74, -27.8) * mm});
            skLineSegment(sketch, "E147", {"start": v(-4.74, -27.8) * mm, "end": v(1.63, -27.8) * mm});
            skLineSegment(sketch, "E148", {"start": v(6.36, -27.8) * mm, "end": v(6.36, -29.38) * mm});
            skLineSegment(sketch, "E149", {"start": v(6.36, -29.38) * mm, "end": v(3.98, -29.38) * mm});
            skLineSegment(sketch, "E150", {"start": v(-7.27, -29.38) * mm, "end": v(-7.27, -28.07) * mm});
            skLineSegment(sketch, "E151", {"start": v(-7.27, -28.07) * mm, "end": v(1.83, -15.35) * mm});
            skLineSegment(sketch, "E152", {"start": v(1.83, -15.35) * mm, "end": v(3.98, -15.35) * mm});
            skLineSegment(sketch, "E153.trimOffspring", {"start": v(3.98, -27.8) * mm, "end": v(6.36, -27.8) * mm});
            skLineSegment(sketch, "E154.trimOffspring", {"start": v(1.63, -29.38) * mm, "end": v(-7.27, -29.38) * mm});
            skLineSegment(sketch, "E155.trimOffspring", {"start": v(1.63, -27.8) * mm, "end": v(1.63, -18.9) * mm});
            skLineSegment(sketch, "E156.trimOffspring", {"start": v(3.98, -29.38) * mm, "end": v(3.98, -34.4) * mm});
            skSolve(sketch);
        }
        {
            var Q0;
            Q0=makeQuery(id+"F35.imprint","IMPRINT",FACE,{"disambiguationData":[TD([[makeQuery(id+"F35.imprint","IMPRINT",EDGE,{"derivedFrom":sQuery(id+"F35.wireOp",EDGE,"E143")}),-1.0]])]});
            extrude(context, id + "F36", {"entities" : qUnion([Q0]), "depth" : 3.5 * mm, "offsetDistance" : 25 * mm});
        }
        {
            var Q0;
            Q0=makeQuery(id+"F36.opExtrude","CAP_FACE",FACE,{"disambiguationData":[OSD([sQuery(id+"F35.wireOp",EDGE,"E143"),sQuery(id+"F35.wireOp",EDGE,"E144"),sQuery(id+"F35.wireOp",EDGE,"E145"),sQuery(id+"F35.wireOp",EDGE,"E146"),sQuery(id+"F35.wireOp",EDGE,"E147"),sQuery(id+"F35.wireOp",EDGE,"E148"),sQuery(id+"F35.wireOp",EDGE,"E149"),sQuery(id+"F35.wireOp",EDGE,"E150"),sQuery(id+"F35.wireOp",EDGE,"E151"),sQuery(id+"F35.wireOp",EDGE,"E152"),sQuery(id+"F35.wireOp",EDGE,"E153.trimOffspring"),sQuery(id+"F35.wireOp",EDGE,"E154.trimOffspring"),sQuery(id+"F35.wireOp",EDGE,"E155.trimOffspring"),sQuery(id+"F35.wireOp",EDGE,"E156.trimOffspring")])],"isStart":true});
            var sketch = newSketch(context, id + "F37", { "sketchPlane" : qUnion([Q0])});
            skCircle(sketch, "E157", {"center": v(-2.58, -17.53) * mm, "radius": 0.95 * mm});
            skCircle(sketch, "E158", {"center": v(-2.81, -28.44) * mm, "radius": 0.95 * mm});
            skSolve(sketch);
        }
        {
            var Q0;
            Q0=makeQuery(id+"F37.imprint","IMPRINT",FACE,{"disambiguationData":[TD([[makeQuery(id+"F37.imprint","IMPRINT",EDGE,{"derivedFrom":sQuery(id+"F37.wireOp",EDGE,"E157")}),1.0]])]});
            var Q1;
            Q1=makeQuery(id+"F37.imprint","IMPRINT",FACE,{"disambiguationData":[TD([[makeQuery(id+"F37.imprint","IMPRINT",EDGE,{"derivedFrom":sQuery(id+"F37.wireOp",EDGE,"E158")}),1.0]])]});
            extrude(context, id + "F38", {"entities" : qUnion([Q0, Q1]), "operationType" : NewBodyOperationType.REMOVE, "oppositeDirection" : true, "depth" : 2.5 * mm, "offsetDistance" : 25 * mm});
        }
        {
            var Q0;
            Q0=qCreatedBy(makeId("Front.planeOp"),FACE);
            var sketch = newSketch(context, id + "F39", { "sketchPlane" : qUnion([Q0])});
            skLineSegment(sketch, "E159", {"start": v(77.45, -18.55) * mm, "end": v(68.9, -18.55) * mm});
            skLineSegment(sketch, "E160", {"start": v(68.9, -18.55) * mm, "end": v(68.9, -16.5) * mm});
            skLineSegment(sketch, "E161", {"start": v(68.9, -16.5) * mm, "end": v(80.12, -16.5) * mm});
            skLineSegment(sketch, "E162", {"start": v(80.12, -16.5) * mm, "end": v(80.12, -18.07) * mm});
            skLineSegment(sketch, "E163", {"start": v(70.5, -35.3) * mm, "end": v(72.5, -35.3) * mm});
            skArc(sketch, "E164", {"start": v(77.45, -18.55) * mm, "mid": v(73.16, -26.58) * mm, "end": v(70.5, -35.3) * mm});
            skArc(sketch, "E165", {"start": v(80.12, -18.07) * mm, "mid": v(75.5, -26.32) * mm, "end": v(72.5, -35.3) * mm});
            skSolve(sketch);
        }
        {
            var Q0;
            Q0=makeQuery(id+"F39.imprint","IMPRINT",FACE,{"disambiguationData":[TD([[makeQuery(id+"F39.imprint","IMPRINT",EDGE,{"derivedFrom":sQuery(id+"F39.wireOp",EDGE,"E159")}),-1.0]])]});
            extrude(context, id + "F40", {"entities" : qUnion([Q0]), "depth" : 3.5 * mm, "offsetDistance" : 25 * mm});
        }
        {
            var Q0;
            Q0=makeQuery(id+"F40.opExtrude","CAP_FACE",FACE,{"disambiguationData":[OSD([sQuery(id+"F39.wireOp",EDGE,"E159"),sQuery(id+"F39.wireOp",EDGE,"E160"),sQuery(id+"F39.wireOp",EDGE,"E161"),sQuery(id+"F39.wireOp",EDGE,"E162"),sQuery(id+"F39.wireOp",EDGE,"E163"),sQuery(id+"F39.wireOp",EDGE,"E164"),sQuery(id+"F39.wireOp",EDGE,"E165")])],"isStart":true});
            var sketch = newSketch(context, id + "F41", { "sketchPlane" : qUnion([Q0])});
            skLineSegment(sketch, "E166.bottom", {"start": v(-75, -16.95) * mm, "end": v(-72.6, -16.95) * mm});
            skLineSegment(sketch, "E166.top", {"start": v(-75, -18.15) * mm, "end": v(-72.6, -18.15) * mm});
            skLineSegment(sketch, "E166.left", {"start": v(-75, -16.95) * mm, "end": v(-75, -18.15) * mm});
            skLineSegment(sketch, "E166.right", {"start": v(-72.6, -16.95) * mm, "end": v(-72.6, -18.15) * mm});
            skLineSegment(sketch, "E167.bottom", {"start": v(-73.84, -26.2) * mm, "end": v(-72.87, -28.4) * mm});
            skLineSegment(sketch, "E167.top", {"start": v(-74.94, -26.69) * mm, "end": v(-73.96, -28.88) * mm});
            skLineSegment(sketch, "E167.left", {"start": v(-73.84, -26.2) * mm, "end": v(-74.94, -26.69) * mm});
            skLineSegment(sketch, "E167.right", {"start": v(-72.87, -28.4) * mm, "end": v(-73.96, -28.88) * mm});
            skSolve(sketch);
        }
        {
            var Q0;
            Q0=makeQuery(id+"F41.imprint","IMPRINT",FACE,{"disambiguationData":[TD([[makeQuery(id+"F41.imprint","IMPRINT",EDGE,{"derivedFrom":sQuery(id+"F41.wireOp",EDGE,"E166.bottom")}),-1.0]])]});
            var Q1;
            Q1=makeQuery(id+"F41.imprint","IMPRINT",FACE,{"disambiguationData":[TD([[makeQuery(id+"F41.imprint","IMPRINT",EDGE,{"derivedFrom":sQuery(id+"F41.wireOp",EDGE,"E167.bottom")}),-1.0]])]});
            extrude(context, id + "F42", {"entities" : qUnion([Q0, Q1]), "operationType" : NewBodyOperationType.REMOVE, "oppositeDirection" : true, "depth" : 2.5 * mm, "offsetDistance" : 25 * mm});
        }
        {
            var Q0;
            Q0=qCreatedBy(makeId("Front.planeOp"),FACE);
            var sketch = newSketch(context, id + "F43", { "sketchPlane" : qUnion([Q0])});
            skCircle(sketch, "E168", {"center": v(51.05, -22.75) * mm, "radius": 6.94 * mm});
            skPoint(sketch, "E168.first.point", {"position": v(51, -15.8) * mm});
            skPoint(sketch, "E168.second.point", {"position": v(45.69, -27.17) * mm});
            skPoint(sketch, "E168.third.point", {"position": v(55.6, -28) * mm});
            skArc(sketch, "E169", {"start": v(55.13, -20.1) * mm, "mid": v(51.07, -17.6) * mm, "end": v(47, -20.1) * mm});
            skArc(sketch, "E170", {"start": v(55.13, -25.4) * mm, "mid": v(55.68, -22.75) * mm, "end": v(55.13, -20.1) * mm});
            skArc(sketch, "E171", {"start": v(47, -25.4) * mm, "mid": v(51.07, -27.9) * mm, "end": v(55.13, -25.4) * mm});
            skArc(sketch, "E172", {"start": v(47, -20.1) * mm, "mid": v(46.43, -22.75) * mm, "end": v(47, -25.4) * mm});
            skSolve(sketch);
        }
        {
            var Q0;
            Q0=makeQuery(id+"F43.imprint","IMPRINT",FACE,{"disambiguationData":[TD([[makeQuery(id+"F43.imprint","IMPRINT",EDGE,{"derivedFrom":sQuery(id+"F43.wireOp",EDGE,"E168")}),1.0]])]});
            extrude(context, id + "F44", {"entities" : qUnion([Q0]), "depth" : 3.5 * mm, "offsetDistance" : 25 * mm});
        }
        {
            var Q0;
            Q0=makeQuery(id+"F44.opExtrude","CAP_FACE",FACE,{"disambiguationData":[OSD([sQuery(id+"F43.wireOp",EDGE,"E168"),sQuery(id+"F43.wireOp",EDGE,"E169"),sQuery(id+"F43.wireOp",EDGE,"E170"),sQuery(id+"F43.wireOp",EDGE,"E171"),sQuery(id+"F43.wireOp",EDGE,"E172")])],"isStart":true});
            var sketch = newSketch(context, id + "F45", { "sketchPlane" : qUnion([Q0])});
            skLineSegment(sketch, "E173.bottom", {"start": v(-46.03, -21.55) * mm, "end": v(-44.83, -21.55) * mm});
            skLineSegment(sketch, "E173.top", {"start": v(-46.03, -23.95) * mm, "end": v(-44.83, -23.95) * mm});
            skLineSegment(sketch, "E173.left", {"start": v(-46.03, -21.55) * mm, "end": v(-46.03, -23.95) * mm});
            skLineSegment(sketch, "E173.right", {"start": v(-44.83, -21.55) * mm, "end": v(-44.83, -23.95) * mm});
            skLineSegment(sketch, "E174.bottom", {"start": v(-57.28, -21.55) * mm, "end": v(-56.08, -21.55) * mm});
            skLineSegment(sketch, "E174.top", {"start": v(-57.28, -23.95) * mm, "end": v(-56.08, -23.95) * mm});
            skLineSegment(sketch, "E174.left", {"start": v(-57.28, -21.55) * mm, "end": v(-57.28, -23.95) * mm});
            skLineSegment(sketch, "E174.right", {"start": v(-56.08, -21.55) * mm, "end": v(-56.08, -23.95) * mm});
            skSolve(sketch);
        }
        {
            var Q0;
            Q0=makeQuery(id+"F45.imprint","IMPRINT",FACE,{"disambiguationData":[TD([[makeQuery(id+"F45.imprint","IMPRINT",EDGE,{"derivedFrom":sQuery(id+"F45.wireOp",EDGE,"jWSxbD9V-05w2-t3B4-b4zD-Bce0T7B3v5nm")}),1.0]])]});
            var Q1;
            Q1=makeQuery(id+"F45.imprint","IMPRINT",FACE,{"disambiguationData":[TD([[makeQuery(id+"F45.imprint","IMPRINT",EDGE,{"derivedFrom":sQuery(id+"F45.wireOp",EDGE,"2D1dj4Iv-WW5q-y8Pl-3n7x-rahMRaiyrRHb")}),1.0]])]});
            var Q2;
            Q2=makeQuery(id+"F45.imprint","IMPRINT",FACE,{"disambiguationData":[TD([[makeQuery(id+"F45.imprint","IMPRINT",EDGE,{"derivedFrom":sQuery(id+"F45.wireOp",EDGE,"E174.bottom")}),-1.0]])]});
            var Q3;
            Q3=makeQuery(id+"F45.imprint","IMPRINT",FACE,{"disambiguationData":[TD([[makeQuery(id+"F45.imprint","IMPRINT",EDGE,{"derivedFrom":sQuery(id+"F45.wireOp",EDGE,"E173.bottom")}),-1.0]])]});
            extrude(context, id + "F46", {"entities" : qUnion([Q0, Q1, Q2, Q3]), "operationType" : NewBodyOperationType.REMOVE, "oppositeDirection" : true, "depth" : 2.5 * mm, "offsetDistance" : 25 * mm});
        }
        {
            var Q0;
            Q0=qCreatedBy(makeId("Front.planeOp"),FACE);
            var sketch = newSketch(context, id + "F47", { "sketchPlane" : qUnion([Q0])});
            skLineSegment(sketch, "E175", {"start": v(-32.6, -34.83) * mm, "end": v(-31.92, -36.07) * mm});
            skArc(sketch, "E176", {"start": v(-31.92, -36.07) * mm, "mid": v(-27.4, -33.47) * mm, "end": v(-23.88, -29.64) * mm});
            skArc(sketch, "E177", {"start": v(-23.88, -29.64) * mm, "mid": v(-22.4, -25.11) * mm, "end": v(-22.58, -20.35) * mm});
            skArc(sketch, "E178", {"start": v(-22.58, -20.35) * mm, "mid": v(-24.48, -17.39) * mm, "end": v(-27.75, -16.08) * mm});
            skArc(sketch, "E179", {"start": v(-27.75, -16.08) * mm, "mid": v(-31.59, -17.06) * mm, "end": v(-33.8, -20.35) * mm});
            skArc(sketch, "E180", {"start": v(-33.8, -20.35) * mm, "mid": v(-34.09, -22.6) * mm, "end": v(-33.8, -24.86) * mm});
            skArc(sketch, "E181", {"start": v(-33.8, -24.86) * mm, "mid": v(-32.49, -26.9) * mm, "end": v(-30.42, -28.18) * mm});
            skArc(sketch, "E182", {"start": v(-30.42, -28.18) * mm, "mid": v(-27.86, -28.35) * mm, "end": v(-25.36, -27.73) * mm});
            skArc(sketch, "E183", {"start": v(-32.6, -34.83) * mm, "mid": v(-28.19, -32.08) * mm, "end": v(-25.36, -27.73) * mm});
            skArc(sketch, "E184", {"start": v(-24.9, -26.21) * mm, "mid": v(-24.66, -23.55) * mm, "end": v(-24.9, -20.88) * mm});
            skArc(sketch, "E185", {"start": v(-24.9, -20.88) * mm, "mid": v(-25.91, -18.76) * mm, "end": v(-27.94, -17.58) * mm});
            skPoint(sketch, "E186", {"position": v(-34.09, -22.6) * mm});
            skPoint(sketch, "E187", {"position": v(-31.68, -22.64) * mm});
            skArc(sketch, "E188", {"start": v(-27.94, -17.58) * mm, "mid": v(-30, -18) * mm, "end": v(-31.34, -19.63) * mm});
            skArc(sketch, "E189", {"start": v(-31.34, -19.63) * mm, "mid": v(-31.68, -22.61) * mm, "end": v(-30.95, -25.53) * mm});
            skArc(sketch, "E190", {"start": v(-30.95, -25.53) * mm, "mid": v(-29.66, -26.77) * mm, "end": v(-27.94, -27.25) * mm});
            skArc(sketch, "E191", {"start": v(-27.94, -27.25) * mm, "mid": v(-26.37, -26.95) * mm, "end": v(-24.92, -26.27) * mm});
            skArc(sketch, "E192.trimOffspring", {"start": v(-24.92, -26.27) * mm, "mid": v(-24.91, -26.24) * mm, "end": v(-24.9, -26.21) * mm});
            skPoint(sketch, "E193.orphan", {"position": v(-23.96, -25.53) * mm});
            skSolve(sketch);
        }
        {
            var Q0;
            Q0=makeQuery(id+"F47.imprint","IMPRINT",FACE,{"disambiguationData":[TD([[makeQuery(id+"F47.imprint","IMPRINT",EDGE,{"derivedFrom":sQuery(id+"F47.wireOp",EDGE,"E175")}),1.0]])]});
            extrude(context, id + "F48", {"entities" : qUnion([Q0]), "depth" : 3.5 * mm, "offsetDistance" : 25 * mm});
        }
        {
            var Q0;
            Q0=makeQuery(id+"F48.opExtrude","CAP_FACE",FACE,{"disambiguationData":[OSD([sQuery(id+"F47.wireOp",EDGE,"E175"),sQuery(id+"F47.wireOp",EDGE,"E176"),sQuery(id+"F47.wireOp",EDGE,"E177"),sQuery(id+"F47.wireOp",EDGE,"E178"),sQuery(id+"F47.wireOp",EDGE,"E179"),sQuery(id+"F47.wireOp",EDGE,"E180"),sQuery(id+"F47.wireOp",EDGE,"E181"),sQuery(id+"F47.wireOp",EDGE,"E182"),sQuery(id+"F47.wireOp",EDGE,"E183"),sQuery(id+"F47.wireOp",EDGE,"E184"),sQuery(id+"F47.wireOp",EDGE,"E185"),sQuery(id+"F47.wireOp",EDGE,"E188"),sQuery(id+"F47.wireOp",EDGE,"E189"),sQuery(id+"F47.wireOp",EDGE,"E190"),sQuery(id+"F47.wireOp",EDGE,"E191"),sQuery(id+"F47.wireOp",EDGE,"E192.trimOffspring")])],"isStart":true});
            var sketch = newSketch(context, id + "F49", { "sketchPlane" : qUnion([Q0])});
            skCircle(sketch, "E194", {"center": v(23.5, -22.6) * mm, "radius": 0.95 * mm});
            skCircle(sketch, "E195", {"center": v(32.88, -22.87) * mm, "radius": 0.95 * mm});
            skSolve(sketch);
        }
        {
            var Q0;
            Q0=makeQuery(id+"F49.imprint","IMPRINT",FACE,{"disambiguationData":[TD([[makeQuery(id+"F49.imprint","IMPRINT",EDGE,{"derivedFrom":sQuery(id+"F49.wireOp",EDGE,"E194")}),1.0]])]});
            var Q1;
            Q1=makeQuery(id+"F49.imprint","IMPRINT",FACE,{"disambiguationData":[TD([[makeQuery(id+"F49.imprint","IMPRINT",EDGE,{"derivedFrom":sQuery(id+"F49.wireOp",EDGE,"E195")}),1.0]])]});
            extrude(context, id + "F50", {"entities" : qUnion([Q0, Q1]), "operationType" : NewBodyOperationType.REMOVE, "oppositeDirection" : true, "depth" : 2.5 * mm, "offsetDistance" : 25 * mm});
        }
        {
            var Q0;
            Q0=qCreatedBy(makeId("Front.planeOp"),FACE);
            var sketch = newSketch(context, id + "F51", { "sketchPlane" : qUnion([Q0])});
            skLineSegment(sketch, "E196", {"start": v(-19.06, -17.35) * mm, "end": v(-18.22, -18.65) * mm});
            skLineSegment(sketch, "E197", {"start": v(-17.14, -24.16) * mm, "end": v(-17.14, -25.79) * mm});
            skLineSegment(sketch, "E198", {"start": v(-19.06, -32.87) * mm, "end": v(-19.75, -34.37) * mm});
            skArc(sketch, "E199", {"start": v(-12.61, -16.41) * mm, "mid": v(-15.95, -16.09) * mm, "end": v(-19.06, -17.35) * mm});
            skArc(sketch, "E200", {"start": v(-10.6, -22.78) * mm, "mid": v(-10.12, -19.12) * mm, "end": v(-12.61, -16.41) * mm});
            skArc(sketch, "E201", {"start": v(-13.75, -24.8) * mm, "mid": v(-11.98, -24.08) * mm, "end": v(-10.6, -22.78) * mm});
            skArc(sketch, "E202", {"start": v(-19.75, -34.37) * mm, "mid": v(-16.24, -35.41) * mm, "end": v(-12.61, -34.9) * mm});
            skArc(sketch, "E203", {"start": v(-12.61, -34.9) * mm, "mid": v(-9.5, -31.3) * mm, "end": v(-10.6, -26.67) * mm});
            skArc(sketch, "E204", {"start": v(-10.6, -26.67) * mm, "mid": v(-12, -25.43) * mm, "end": v(-13.75, -24.8) * mm});
            skArc(sketch, "E205", {"start": v(-13.75, -18.1) * mm, "mid": v(-16.05, -17.8) * mm, "end": v(-18.22, -18.65) * mm});
            skArc(sketch, "E206", {"start": v(-13.75, -23.42) * mm, "mid": v(-12.26, -20.76) * mm, "end": v(-13.75, -18.1) * mm});
            skLineSegment(sketch, "E207", {"start": v(-17.14, -24.16) * mm, "end": v(-16.1, -24.16) * mm});
            skLineSegment(sketch, "E208", {"start": v(-17.14, -25.79) * mm, "end": v(-16.1, -25.79) * mm});
            skArc(sketch, "E209", {"start": v(-16.1, -24.16) * mm, "mid": v(-14.87, -23.97) * mm, "end": v(-13.75, -23.42) * mm});
            skArc(sketch, "E210", {"start": v(-11.68, -29.94) * mm, "mid": v(-13.07, -26.99) * mm, "end": v(-16.1, -25.79) * mm});
            skArc(sketch, "E211", {"start": v(-19.06, -32.87) * mm, "mid": v(-16.72, -33.52) * mm, "end": v(-14.29, -33.48) * mm});
            skArc(sketch, "E212", {"start": v(-14.29, -33.48) * mm, "mid": v(-12.26, -32.25) * mm, "end": v(-11.68, -29.94) * mm});
            skSolve(sketch);
        }
        {
            var Q0;
            Q0=makeQuery(id+"F51.imprint","IMPRINT",FACE,{"disambiguationData":[TD([[makeQuery(id+"F51.imprint","IMPRINT",EDGE,{"derivedFrom":sQuery(id+"F51.wireOp",EDGE,"E196")}),1.0]])]});
            extrude(context, id + "F52", {"entities" : qUnion([Q0]), "depth" : 3.5 * mm, "offsetDistance" : 25 * mm});
        }
        {
            var Q0;
            Q0=qCreatedBy(makeId("Front.planeOp"),FACE);
            var sketch = newSketch(context, id + "F53", { "sketchPlane" : qUnion([Q0])});
            skLineSegment(sketch, "E213.bottom", {"start": v(14.61, -21.22) * mm, "end": v(21.72, -21.22) * mm});
            skLineSegment(sketch, "E213.top", {"start": v(14.61, -23.3) * mm, "end": v(21.72, -23.3) * mm});
            skLineSegment(sketch, "E213.left", {"start": v(14.61, -21.22) * mm, "end": v(14.61, -23.3) * mm});
            skLineSegment(sketch, "E213.right", {"start": v(21.72, -21.22) * mm, "end": v(21.72, -23.3) * mm});
            skSolve(sketch);
        }
        {
            var Q0;
            Q0=makeQuery(id+"F53.imprint","IMPRINT",FACE,{"disambiguationData":[TD([[makeQuery(id+"F53.imprint","IMPRINT",EDGE,{"derivedFrom":sQuery(id+"F53.wireOp",EDGE,"E213.bottom")}),-1.0]])]});
            extrude(context, id + "F54", {"entities" : qUnion([Q0]), "depth" : 3.5 * mm, "offsetDistance" : 25 * mm});
        }
        {
            var Q0;
            Q0=makeQuery(id+"F54.opExtrude","CAP_FACE",FACE,{"disambiguationData":[OSD([sQuery(id+"F53.wireOp",EDGE,"E213.bottom"),sQuery(id+"F53.wireOp",EDGE,"E213.top"),sQuery(id+"F53.wireOp",EDGE,"E213.left"),sQuery(id+"F53.wireOp",EDGE,"E213.right")])],"isStart":true});
            var sketch = newSketch(context, id + "F55", { "sketchPlane" : qUnion([Q0])});
            skLineSegment(sketch, "E214.bottom", {"start": v(-19.45, -21.67) * mm, "end": v(-17.05, -21.67) * mm});
            skLineSegment(sketch, "E214.top", {"start": v(-19.45, -22.87) * mm, "end": v(-17.05, -22.87) * mm});
            skLineSegment(sketch, "E214.left", {"start": v(-19.45, -21.67) * mm, "end": v(-19.45, -22.87) * mm});
            skLineSegment(sketch, "E214.right", {"start": v(-17.05, -21.67) * mm, "end": v(-17.05, -22.87) * mm});
            skSolve(sketch);
        }
        {
            var Q0;
            Q0=makeQuery(id+"F55.imprint","IMPRINT",FACE,{"disambiguationData":[TD([[makeQuery(id+"F55.imprint","IMPRINT",EDGE,{"derivedFrom":sQuery(id+"F55.wireOp",EDGE,"E214.bottom")}),-1.0]])]});
            extrude(context, id + "F56", {"entities" : qUnion([Q0]), "operationType" : NewBodyOperationType.REMOVE, "oppositeDirection" : true, "depth" : 2.5 * mm, "offsetDistance" : 25 * mm});
        }
        {
            var Q0;
            Q0=qCreatedBy(makeId("Front.planeOp"),FACE);
            var sketch = newSketch(context, id + "F57", { "sketchPlane" : qUnion([Q0])});
            skLineSegment(sketch, "E215", {"start": v(31.67, -28.2) * mm, "end": v(31.67, -29.34) * mm});
            skLineSegment(sketch, "E216", {"start": v(31.67, -29.34) * mm, "end": v(41.55, -29.34) * mm});
            skLineSegment(sketch, "E217", {"start": v(41.55, -29.34) * mm, "end": v(41.55, -27.55) * mm});
            skLineSegment(sketch, "E218", {"start": v(41.55, -27.55) * mm, "end": v(35.03, -27.55) * mm});
            skLineSegment(sketch, "E219", {"start": v(31.63, -17.67) * mm, "end": v(32.7, -19.2) * mm});
            skLineSegment(sketch, "E220", {"start": v(31.67, -28.2) * mm, "end": v(36.88, -23.82) * mm});
            skLineSegment(sketch, "E221", {"start": v(35.03, -27.55) * mm, "end": v(38.33, -24.95) * mm});
            skArc(sketch, "E222", {"start": v(41.22, -22.06) * mm, "mid": v(41.06, -18.32) * mm, "end": v(38.05, -16.08) * mm});
            skArc(sketch, "E223", {"start": v(39.1, -21.51) * mm, "mid": v(39.18, -19.3) * mm, "end": v(37.5, -17.84) * mm});
            skArc(sketch, "E224", {"start": v(38.05, -16.08) * mm, "mid": v(34.67, -16.17) * mm, "end": v(31.63, -17.67) * mm});
            skArc(sketch, "E225", {"start": v(38.33, -24.95) * mm, "mid": v(39.86, -23.59) * mm, "end": v(41.22, -22.06) * mm});
            skArc(sketch, "E226", {"start": v(36.88, -23.82) * mm, "mid": v(38.06, -22.72) * mm, "end": v(39.1, -21.51) * mm});
            skArc(sketch, "E227", {"start": v(37.5, -17.84) * mm, "mid": v(34.92, -17.84) * mm, "end": v(32.7, -19.2) * mm});
            skSolve(sketch);
        }
        {
            var Q0;
            Q0=makeQuery(id+"F57.imprint","IMPRINT",FACE,{"disambiguationData":[TD([[makeQuery(id+"F57.imprint","IMPRINT",EDGE,{"derivedFrom":sQuery(id+"F57.wireOp",EDGE,"E215")}),1.0]])]});
            extrude(context, id + "F58", {"entities" : qUnion([Q0]), "depth" : 3.5 * mm, "offsetDistance" : 25 * mm});
        }
        {
            var Q0;
            Q0=makeQuery(id+"F58.opExtrude","SWEPT_EDGE",EDGE,{"disambiguationData":[OSD([sQuery(id+"F57.wireOp",EDGE,"E222"),sQuery(id+"F57.wireOp",EDGE,"E225")])]});
            fillet(context, id + "F59", {"entities" : qUnion([Q0]), "radius" : 4 * mm, "tangentPropagation" : true, "allowEdgeOverflow" : false});
        }
        {
            var Q0;
            Q0=makeQuery(id+"F58.opExtrude","SWEPT_EDGE",EDGE,{"disambiguationData":[OSD([sQuery(id+"F57.wireOp",EDGE,"E223"),sQuery(id+"F57.wireOp",EDGE,"E226")])]});
            fillet(context, id + "F60", {"entities" : qUnion([Q0]), "radius" : 2.12 * mm, "tangentPropagation" : true, "allowEdgeOverflow" : false});
        }
        {
            var Q0;
            Q0=makeQuery(id+"F58.opExtrude","CAP_FACE",FACE,{"disambiguationData":[OSD([sQuery(id+"F57.wireOp",EDGE,"E215"),sQuery(id+"F57.wireOp",EDGE,"E216"),sQuery(id+"F57.wireOp",EDGE,"E217"),sQuery(id+"F57.wireOp",EDGE,"E218"),sQuery(id+"F57.wireOp",EDGE,"E219"),sQuery(id+"F57.wireOp",EDGE,"E220"),sQuery(id+"F57.wireOp",EDGE,"E221"),sQuery(id+"F57.wireOp",EDGE,"E222"),sQuery(id+"F57.wireOp",EDGE,"E223"),sQuery(id+"F57.wireOp",EDGE,"E224"),sQuery(id+"F57.wireOp",EDGE,"E225"),sQuery(id+"F57.wireOp",EDGE,"E226"),sQuery(id+"F57.wireOp",EDGE,"E227")])],"isStart":true});
            var sketch = newSketch(context, id + "F61", { "sketchPlane" : qUnion([Q0])});
            skLineSegment(sketch, "E228.bottom", {"start": v(-38.45, -27.9) * mm, "end": v(-36.05, -27.9) * mm});
            skLineSegment(sketch, "E228.top", {"start": v(-38.45, -29.1) * mm, "end": v(-36.05, -29.1) * mm});
            skLineSegment(sketch, "E228.left", {"start": v(-38.45, -27.9) * mm, "end": v(-38.45, -29.1) * mm});
            skLineSegment(sketch, "E228.right", {"start": v(-36.05, -27.9) * mm, "end": v(-36.05, -29.1) * mm});
            skLineSegment(sketch, "E229.bottom", {"start": v(-38.52, -17.77) * mm, "end": v(-40.07, -19.6) * mm});
            skLineSegment(sketch, "E229.top", {"start": v(-39.44, -17) * mm, "end": v(-40.98, -18.83) * mm});
            skLineSegment(sketch, "E229.left", {"start": v(-38.52, -17.77) * mm, "end": v(-39.44, -17) * mm});
            skLineSegment(sketch, "E229.right", {"start": v(-40.07, -19.6) * mm, "end": v(-40.98, -18.83) * mm});
            skPoint(sketch, "E229.middle", {"position": v(-39.75, -18.3) * mm});
            skSolve(sketch);
        }
        {
            var Q0;
            Q0=makeQuery(id+"F61.imprint","IMPRINT",FACE,{"disambiguationData":[TD([[makeQuery(id+"F61.imprint","IMPRINT",EDGE,{"derivedFrom":sQuery(id+"F61.wireOp",EDGE,"E229.bottom")}),-1.0]])]});
            var Q1;
            Q1=makeQuery(id+"F61.imprint","IMPRINT",FACE,{"disambiguationData":[TD([[makeQuery(id+"F61.imprint","IMPRINT",EDGE,{"derivedFrom":sQuery(id+"F61.wireOp",EDGE,"E228.bottom")}),-1.0]])]});
            extrude(context, id + "F62", {"entities" : qUnion([Q0, Q1]), "operationType" : NewBodyOperationType.REMOVE, "oppositeDirection" : true, "depth" : 2.5 * mm, "offsetDistance" : 25 * mm});
        }
        {
            var Q0;
            Q0=makeQuery(id+"F52.opExtrude","CAP_FACE",FACE,{"disambiguationData":[OSD([sQuery(id+"F51.wireOp",EDGE,"E196"),sQuery(id+"F51.wireOp",EDGE,"E197"),sQuery(id+"F51.wireOp",EDGE,"E198"),sQuery(id+"F51.wireOp",EDGE,"E199"),sQuery(id+"F51.wireOp",EDGE,"E200"),sQuery(id+"F51.wireOp",EDGE,"E201"),sQuery(id+"F51.wireOp",EDGE,"E202"),sQuery(id+"F51.wireOp",EDGE,"E203"),sQuery(id+"F51.wireOp",EDGE,"E204"),sQuery(id+"F51.wireOp",EDGE,"E205"),sQuery(id+"F51.wireOp",EDGE,"E206"),sQuery(id+"F51.wireOp",EDGE,"E207"),sQuery(id+"F51.wireOp",EDGE,"E208"),sQuery(id+"F51.wireOp",EDGE,"E209"),sQuery(id+"F51.wireOp",EDGE,"E210"),sQuery(id+"F51.wireOp",EDGE,"E211"),sQuery(id+"F51.wireOp",EDGE,"E212")])],"isStart":true});
            var sketch = newSketch(context, id + "F63", { "sketchPlane" : qUnion([Q0])});
            skLineSegment(sketch, "E230.bottom", {"start": v(10.72, -19.21) * mm, "end": v(11.92, -19.21) * mm});
            skLineSegment(sketch, "E230.top", {"start": v(10.72, -21.61) * mm, "end": v(11.92, -21.61) * mm});
            skLineSegment(sketch, "E230.left", {"start": v(10.72, -19.21) * mm, "end": v(10.72, -21.61) * mm});
            skLineSegment(sketch, "E230.right", {"start": v(11.92, -19.21) * mm, "end": v(11.92, -21.61) * mm});
            skLineSegment(sketch, "E231.bottom", {"start": v(10.07, -28.77) * mm, "end": v(11.27, -28.77) * mm});
            skLineSegment(sketch, "E231.top", {"start": v(10.07, -31.17) * mm, "end": v(11.27, -31.17) * mm});
            skLineSegment(sketch, "E231.left", {"start": v(10.07, -28.77) * mm, "end": v(10.07, -31.17) * mm});
            skLineSegment(sketch, "E231.right", {"start": v(11.27, -28.77) * mm, "end": v(11.27, -31.17) * mm});
            skSolve(sketch);
        }
        {
            var Q0;
            Q0=makeQuery(id+"F63.imprint","IMPRINT",FACE,{"disambiguationData":[TD([[makeQuery(id+"F63.imprint","IMPRINT",EDGE,{"derivedFrom":sQuery(id+"F63.wireOp",EDGE,"E230.bottom")}),-1.0]])]});
            var Q1;
            Q1=makeQuery(id+"F63.imprint","IMPRINT",FACE,{"disambiguationData":[TD([[makeQuery(id+"F63.imprint","IMPRINT",EDGE,{"derivedFrom":sQuery(id+"F63.wireOp",EDGE,"E231.bottom")}),-1.0]])]});
            extrude(context, id + "F64", {"entities" : qUnion([Q0, Q1]), "operationType" : NewBodyOperationType.REMOVE, "oppositeDirection" : true, "depth" : 2.5 * mm, "offsetDistance" : 25 * mm});
        }
    });
